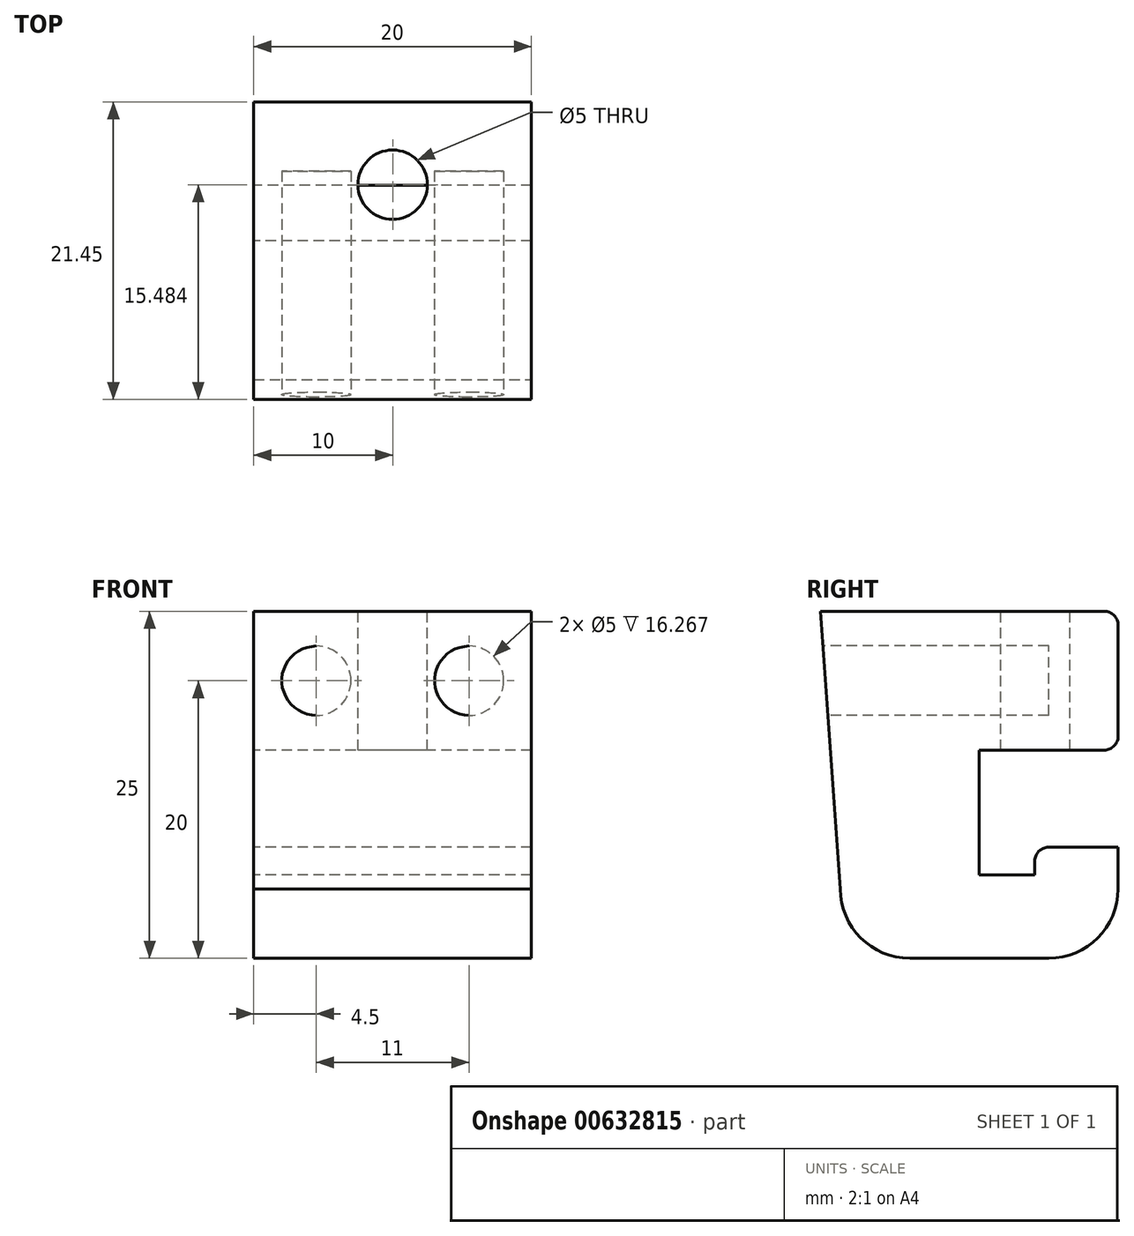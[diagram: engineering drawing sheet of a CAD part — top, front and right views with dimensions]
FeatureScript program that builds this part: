
annotation { "Feature Type Name" : "Feature", "Feature Type Description" : "" }
export const myFeature = defineFeature(function(context is Context, id is Id, definition is map)
    precondition{}
    {
        {
            var Q0;
            Q0=qCreatedBy(makeId("Top.planeOp"),FACE);
            var sketch = newSketch(context, id + "F0", { "sketchPlane" : qUnion([Q0])});
            skLineSegment(sketch, "E0.bottom", {"start": v(-10, 10) * mm, "end": v(10, 10) * mm});
            skLineSegment(sketch, "E0.top", {"start": v(-10, -10) * mm, "end": v(10, -10) * mm});
            skLineSegment(sketch, "E0.left", {"start": v(-10, 10) * mm, "end": v(-10, -10) * mm});
            skLineSegment(sketch, "E0.right", {"start": v(10, 10) * mm, "end": v(10, -10) * mm});
            skSolve(sketch);
        }
        {
            var Q0;
            Q0=makeQuery(id+"F0.imprint","IMPRINT",FACE,{"disambiguationData":[TD([[makeQuery(id+"F0.imprint","IMPRINT",EDGE,{"derivedFrom":sQuery(id+"F0.wireOp",EDGE,"E0.bottom")}),-1.0]])]});
            extrude(context, id + "F1", {"entities" : qUnion([Q0]), "depth" : 25 * mm, "offsetDistance" : 25 * mm});
        }
        {
            var Q0;
            Q0=makeQuery(id+"F1.opExtrude","SWEPT_FACE",FACE,{"disambiguationData":[OSD([sQuery(id+"F0.wireOp",EDGE,"E0.left")])]});
            var sketch = newSketch(context, id + "F2", { "sketchPlane" : qUnion([Q0])});
            skLineSegment(sketch, "E1.bottom", {"start": v(-10, 15) * mm, "end": v(0, 15) * mm});
            skLineSegment(sketch, "E1.top", {"start": v(-10, 8) * mm, "end": v(-4, 8) * mm});
            skLineSegment(sketch, "E1.left", {"start": v(-10, 15) * mm, "end": v(-10, 8) * mm});
            skLineSegment(sketch, "E1.right", {"start": v(0, 15) * mm, "end": v(0, 8) * mm});
            skLineSegment(sketch, "E2.top", {"start": v(0, 6) * mm, "end": v(-4, 6) * mm});
            skLineSegment(sketch, "E2.left", {"start": v(0, 8) * mm, "end": v(0, 6) * mm});
            skLineSegment(sketch, "E2.right", {"start": v(-4, 8) * mm, "end": v(-4, 6) * mm});
            skSolve(sketch);
        }
        {
            var Q0;
            Q0=makeQuery(id+"F2.imprint","IMPRINT",FACE,{"disambiguationData":[TD([[makeQuery(id+"F2.imprint","IMPRINT",EDGE,{"derivedFrom":sQuery(id+"F2.wireOp",EDGE,"E1.bottom")}),-1.0]])]});
            extrude(context, id + "F3", {"entities" : qUnion([Q0]), "operationType" : NewBodyOperationType.REMOVE, "oppositeDirection" : true, "depth" : 25 * mm, "offsetDistance" : 25 * mm});
        }
        {
            var Q0;
            Q0=makeQuery(id+"F1.opExtrude","CAP_FACE",FACE,{"disambiguationData":[OSD([sQuery(id+"F0.wireOp",EDGE,"E0.bottom"),sQuery(id+"F0.wireOp",EDGE,"E0.top"),sQuery(id+"F0.wireOp",EDGE,"E0.left"),sQuery(id+"F0.wireOp",EDGE,"E0.right")])],"isStart":false});
            var sketch = newSketch(context, id + "F4", { "sketchPlane" : qUnion([Q0])});
            skCircle(sketch, "E3", {"center": v(0, 4.03) * mm, "radius": 2.5 * mm});
            skSolve(sketch);
        }
        {
            var Q0;
            Q0=makeQuery(id+"F4.imprint","IMPRINT",FACE,{"disambiguationData":[TD([[makeQuery(id+"F4.imprint","IMPRINT",EDGE,{"derivedFrom":sQuery(id+"F4.wireOp",EDGE,"E3")}),1.0]])]});
            extrude(context, id + "F5", {"entities" : qUnion([Q0]), "operationType" : NewBodyOperationType.REMOVE, "oppositeDirection" : true, "depth" : 10 * mm, "offsetDistance" : 25 * mm});
        }
        {
            var Q0;
            Q0=makeQuery(id+"F1.opExtrude","SWEPT_FACE",FACE,{"disambiguationData":[OSD([sQuery(id+"F0.wireOp",EDGE,"E0.top")])]});
            var sketch = newSketch(context, id + "F6", { "sketchPlane" : qUnion([Q0])});
            skCircle(sketch, "E4", {"center": v(-5.5, 20) * mm, "radius": 2.5 * mm});
            skCircle(sketch, "E5", {"center": v(5.5, 20) * mm, "radius": 2.5 * mm});
            skSolve(sketch);
        }
        {
            var Q0;
            Q0=makeQuery(id+"F1.opExtrude","CAP_EDGE",EDGE,{"disambiguationData":[OSD([sQuery(id+"F0.wireOp",EDGE,"E0.bottom")])],"isStart":true});
            var Q1;
            Q1=makeQuery(id+"F1.opExtrude","CAP_EDGE",EDGE,{"disambiguationData":[OSD([sQuery(id+"F0.wireOp",EDGE,"E0.top")])],"isStart":true});
            fillet(context, id + "F7", {"entities" : qUnion([Q0, Q1]), "radius" : 5 * mm, "tangentPropagation" : true, "allowEdgeOverflow" : false});
        }
        {
            var Q0;
            Q0=makeQuery(id+"F3.boolean.opBoolean","COPY",EDGE,{"derivedFrom":makeQuery(id+"F3.opExtrude","SWEPT_EDGE",EDGE,{"disambiguationData":[OSD([sQuery(id+"F0.wireOp",EDGE,"E0.bottom"),sQuery(id+"F0.wireOp",EDGE,"E0.left"),sQuery(id+"F2.wireOp",EDGE,"E1.bottom"),sQuery(id+"F2.wireOp",EDGE,"E1.left")])]})});
            var Q1;
            Q1=makeQuery(id+"F3.boolean.opBoolean","COPY",EDGE,{"derivedFrom":makeQuery(id+"F3.opExtrude","SWEPT_EDGE",EDGE,{"disambiguationData":[OSD([sQuery(id+"F0.wireOp",EDGE,"E0.bottom"),sQuery(id+"F0.wireOp",EDGE,"E0.left"),sQuery(id+"F2.wireOp",EDGE,"E1.top"),sQuery(id+"F2.wireOp",EDGE,"E1.left")])]})});
            var Q2;
            Q2=makeQuery(id+"F1.opExtrude","CAP_EDGE",EDGE,{"disambiguationData":[OSD([sQuery(id+"F0.wireOp",EDGE,"E0.bottom")])],"isStart":false});
            var Q3;
            Q3=makeQuery(id+"F3.boolean.opBoolean","COPY",EDGE,{"derivedFrom":makeQuery(id+"F3.opExtrude","SWEPT_EDGE",EDGE,{"disambiguationData":[OSD([sQuery(id+"F2.wireOp",EDGE,"E1.top"),sQuery(id+"F2.wireOp",EDGE,"E2.right")])]})});
            fillet(context, id + "F8", {"entities" : qUnion([Q0, Q1, Q2, Q3]), "radius" : 1 * mm, "tangentPropagation" : true, "allowEdgeOverflow" : false});
        }
        {
            var Q0;
            Q0=makeQuery(id+"F1.opExtrude","SWEPT_FACE",FACE,{"disambiguationData":[OSD([sQuery(id+"F0.wireOp",EDGE,"E0.left")])]});
            var sketch = newSketch(context, id + "F9", { "sketchPlane" : qUnion([Q0])});
            skLineSegment(sketch, "E6", {"start": v(10, 25) * mm, "end": v(10, 5) * mm});
            skLineSegment(sketch, "E7", {"start": v(10, 5) * mm, "end": v(11.45, 25) * mm});
            skLineSegment(sketch, "E8", {"start": v(10, 25) * mm, "end": v(11.45, 25) * mm});
            skSolve(sketch);
        }
        {
            var Q0;
            Q0=makeQuery(id+"F9.imprint","IMPRINT",FACE,{"disambiguationData":[TD([[makeQuery(id+"F9.imprint","IMPRINT",EDGE,{"derivedFrom":sQuery(id+"F9.wireOp",EDGE,"E6")}),1.0]])]});
            extrude(context, id + "F10", {"entities" : qUnion([Q0]), "operationType" : NewBodyOperationType.ADD, "oppositeDirection" : true, "depth" : 20 * mm, "offsetDistance" : 25 * mm});
        }
        {
            var Q0;
            Q0=makeQuery(id+"F6.imprint","IMPRINT",FACE,{"disambiguationData":[TD([[makeQuery(id+"F6.imprint","IMPRINT",EDGE,{"derivedFrom":sQuery(id+"F6.wireOp",EDGE,"E4")}),1.0]])]});
            var Q1;
            Q1=makeQuery(id+"F6.imprint","IMPRINT",FACE,{"disambiguationData":[TD([[makeQuery(id+"F6.imprint","IMPRINT",EDGE,{"derivedFrom":sQuery(id+"F6.wireOp",EDGE,"E5")}),1.0]])]});
            extrude(context, id + "F11", {"entities" : qUnion([Q0, Q1]), "operationType" : NewBodyOperationType.REMOVE, "oppositeDirection" : true, "depth" : 15 * mm, "offsetDistance" : 25 * mm, "hasSecondDirection" : true, "secondDirectionOppositeDirection" : false, "secondDirectionDepth" : 25 * mm});
        }
    });
